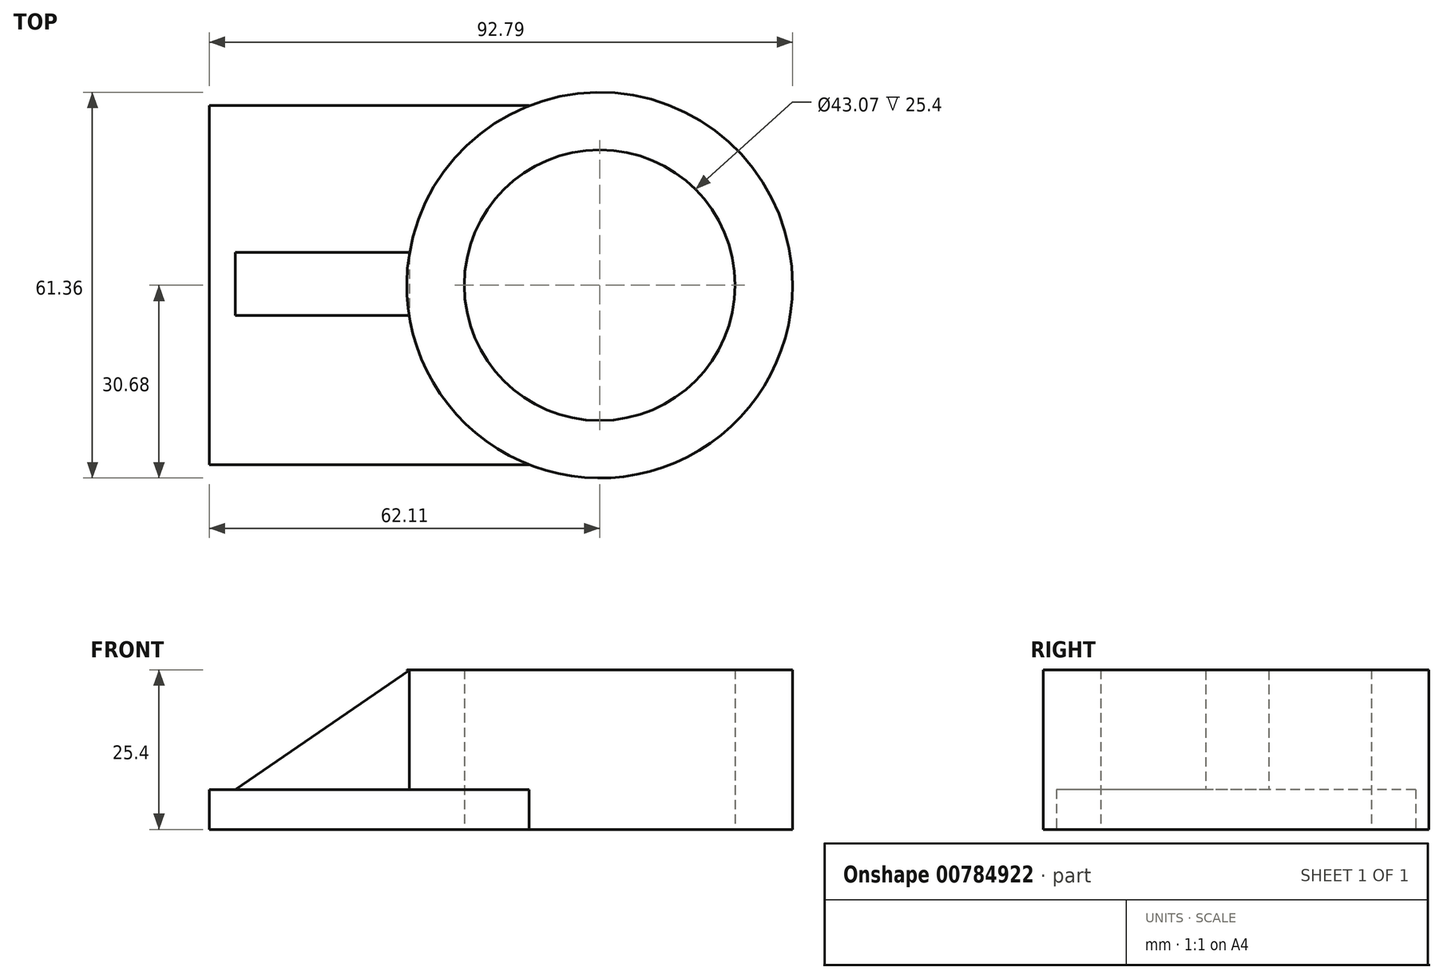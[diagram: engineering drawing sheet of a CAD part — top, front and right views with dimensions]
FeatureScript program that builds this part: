
annotation { "Feature Type Name" : "Feature", "Feature Type Description" : "" }
export const myFeature = defineFeature(function(context is Context, id is Id, definition is map)
    precondition{}
    {
        {
            var Q0;
            Q0=qCreatedBy(makeId("Top.planeOp"),FACE);
            var sketch = newSketch(context, id + "F0", { "sketchPlane" : qUnion([Q0])});
            skCircle(sketch, "E0", {"center": v(0, 0) * mm, "radius": 30.68 * mm});
            skCircle(sketch, "E1", {"center": v(0, 0) * mm, "radius": 21.54 * mm});
            skLineSegment(sketch, "E2", {"start": v(-11.21, -28.56) * mm, "end": v(-62.11, -28.56) * mm});
            skLineSegment(sketch, "E3", {"start": v(-11.21, 28.56) * mm, "end": v(-62.11, 28.56) * mm});
            skLineSegment(sketch, "E4", {"start": v(-62.11, 28.56) * mm, "end": v(-62.11, -28.56) * mm});
            skSolve(sketch);
        }
        {
            var Q0;
            {var subQ0=sQuery(id+"F0.wireOp",EDGE,"E2");Q0=makeQuery(id+"F0.imprint","IMPRINT",FACE,{"disambiguationData":[TD([[makeQuery(id+"F0.imprint","IMPRINT",EDGE,{"derivedFrom":subQ0}),-1.0]])]});}
            extrude(context, id + "F1", {"entities" : qUnion([Q0]), "depth" : 6.35 * mm, "offsetDistance" : 25.4 * mm});
        }
        {
            var Q0;
            Q0=makeQuery(id+"F0.imprint","IMPRINT",FACE,{"disambiguationData":[TD([[makeQuery(id+"F0.imprint","IMPRINT",EDGE,{"derivedFrom":sQuery(id+"F0.wireOp",EDGE,"E1")}),-1.0]])]});
            extrude(context, id + "F2", {"entities" : qUnion([Q0]), "operationType" : NewBodyOperationType.ADD, "depth" : 25.4 * mm, "offsetDistance" : 25.4 * mm});
        }
        {
            var Q0;
            Q0=makeQuery(id+"F1.opExtrude","CAP_FACE",FACE,{"disambiguationData":[OSD([sQuery(id+"F0.wireOp",EDGE,"E0"),sQuery(id+"F0.wireOp",EDGE,"E2"),sQuery(id+"F0.wireOp",EDGE,"E3"),sQuery(id+"F0.wireOp",EDGE,"E4")])],"isStart":false});
            var sketch = newSketch(context, id + "F3", { "sketchPlane" : qUnion([Q0])});
            skLineSegment(sketch, "E5.bottom", {"start": v(-30.24, 5.2) * mm, "end": v(-57.99, 5.2) * mm});
            skLineSegment(sketch, "E5.top", {"start": v(-30.24, -4.79) * mm, "end": v(-57.99, -4.79) * mm});
            skLineSegment(sketch, "E5.left", {"start": v(-30.24, 5.2) * mm, "end": v(-30.24, -4.79) * mm});
            skLineSegment(sketch, "E5.right", {"start": v(-57.99, 5.2) * mm, "end": v(-57.99, -4.79) * mm});
            skSolve(sketch);
        }
        {
            var Q0;
            Q0 = qSketchRegion(id + "F3", true);
            extrude(context, id + "F4", {"entities" : qUnion([Q0]), "operationType" : NewBodyOperationType.ADD, "depth" : 18.95 * mm, "offsetDistance" : 25.4 * mm});
        }
        {
            var Q0;
            Q0=makeQuery(id+"F4.opExtrude","SWEPT_FACE",FACE,{"disambiguationData":[OSD([sQuery(id+"F3.wireOp",EDGE,"E5.top")])]});
            var sketch = newSketch(context, id + "F5", { "sketchPlane" : qUnion([Q0])});
            skLineSegment(sketch, "E6", {"start": v(-30.3, 25.3) * mm, "end": v(-57.99, 6.35) * mm});
            skSolve(sketch);
        }
        {
            var Q0;
            Q0=makeQuery(id+"F5.imprint","IMPRINT",FACE,{"disambiguationData":[TD([[makeQuery(id+"F5.imprint","IMPRINT",EDGE,{"derivedFrom":sQuery(id+"F5.wireOp",EDGE,"E6")}),-1.0]])]});
            extrude(context, id + "F6", {"entities" : qUnion([Q0]), "operationType" : NewBodyOperationType.REMOVE, "oppositeDirection" : true, "depth" : 25.4 * mm, "offsetDistance" : 25.4 * mm});
        }
    });
